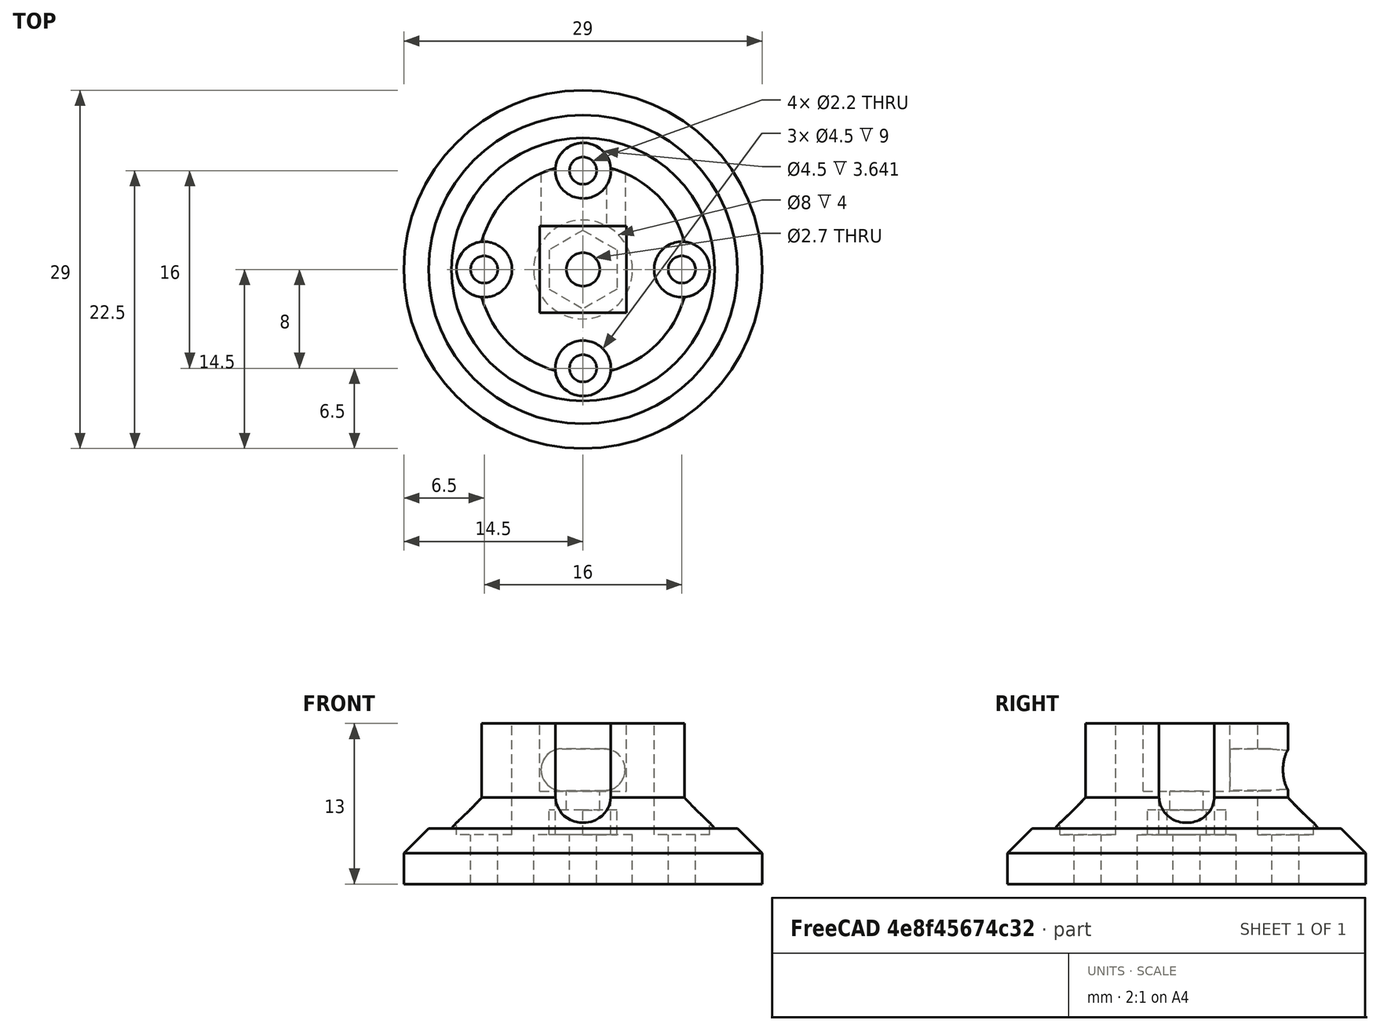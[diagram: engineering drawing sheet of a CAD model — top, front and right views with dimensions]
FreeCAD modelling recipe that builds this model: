
FCSTD DOCUMENT  (FreeCAD 0.14R2935 (Git))
Label: tendon_wheel_ax_9_15_mm
License: CC-BY 3.0
LicenseURL: http://creativecommons.org/licenses/by/3.0/
objects: Part::Cylinder×14, Part::MultiFuse×6, Part::Box×2, Part::Cone×1, Part::Extrusion×1, Part::Mirroring×1, Part::Cut×1, Part::Chamfer×1
note: 27 computed .brp shape members not serialized (recipe doc carries the construction recipe); baked Part::Feature solids carry a one-line shape summary decoded from their .brp

FEATURE [Part::Cylinder] Cylinder
  Angle = 360
  Height = 4.5
  Placement = pos=(0,0,0.5) rot=(0,0,1;0rad)
  Radius = 14.5
FEATURE [Part::Cone] Cone
  Angle = 360
  Height = 3.5
  Placement = pos=(0,0,4) rot=(0,0,1;0rad)
  Radius1 = 11.5
  Radius2 = 8.5
FEATURE [Part::Cylinder] Cylinder001
  Angle = 360
  Height = 6.5
  Placement = pos=(0,0,7) rot=(0,0,1;0rad)
  Radius = 8.5
FEATURE [Part::Cylinder] Cylinder003  label="TopHole003"
  Angle = 360
  Height = 20
  Placement = pos=(-8,0,-3) rot=(0,0,1;0rad)
  Radius = 1.1
FEATURE [Part::Cylinder] Cylinder004  label="TopHole002"
  Angle = 360
  Height = 20
  Placement = pos=(0,-8,-3) rot=(0,0,1;0rad)
  Radius = 1.1
FEATURE [Part::Cylinder] Cylinder005  label="TopHole001"
  Angle = 360
  Height = 20
  Placement = pos=(8,0,-3) rot=(0,0,1;0rad)
  Radius = 1.1
FEATURE [Part::Cylinder] Cylinder006  label="TopHole"
  Angle = 360
  Height = 10
  Placement = pos=(0,8,-3) rot=(0,0,1;0rad)
  Radius = 1.1
FEATURE [Part::Cylinder] Cylinder007  label="TopHole004"
  Angle = 360
  Height = 20
  Placement = pos=(-8,0,3.5) rot=(0,0,1;0rad)
  Radius = 2.25
FEATURE [Part::Cylinder] Cylinder008  label="TopHole005"
  Angle = 360
  Height = 20
  Placement = pos=(8,0,3.5) rot=(0,0,1;0rad)
  Radius = 2.25
FEATURE [Part::Cylinder] Cylinder009  label="TopHole006"
  Angle = 360
  Height = 20
  Placement = pos=(0,8,3.5) rot=(0,0,1;0rad)
  Radius = 2.25
FEATURE [Part::Cylinder] Cylinder010  label="TopHole007"
  Angle = 360
  Height = 20
  Placement = pos=(0,-8,3.5) rot=(0,0,1;0rad)
  Radius = 2.25
FEATURE [Part::MultiFuse] Fusion001
  Placement = pos=(0,0,1) rot=(0,0,1;0rad)
  Shapes = -> [Cylinder010,Cylinder007,Cylinder005,Cylinder003,Cylinder009,Cylinder004,Cylinder008,Cylinder006]
FEATURE [Part::Cylinder] Cylinder012  label="Cylinder003"
  Angle = 360
  Height = 10
  Placement = pos=(-1.7,12,9.75) rot=(1,0,0;1.5708rad)
  Radius = 1.7
FEATURE [Part::Cylinder] Cylinder013  label="Cylinder004"
  Angle = 360
  Height = 20
  Placement = pos=(0,0,-5) rot=(0,0,1;0rad)
  Radius = 1.35
FEATURE [Part::Box] Box  label="Cube"
  Height = 8
  Length = 7
  Placement = pos=(-3.5,-3.5,8) rot=(0,0,1;0rad)
  Width = 7
FEATURE [Part::Extrusion] Extrude
  Dir = (0,0,2)
  Solid = true
FEATURE [Part::Mirroring] Part__Mirroring  label="Extrude (Mirror #1)"
  Base = (0,0,0)
  Normal = (1,0,0)
  Source = -> Extrude
FEATURE [Part::MultiFuse] Fusion002
  Placement = pos=(0,0,4.5) rot=(0,0,1;0rad)
  Shapes = -> [Part__Mirroring,Extrude]
FEATURE [Part::Cylinder] Cylinder014  label="Cylinder005"
  Angle = 360
  Height = 4.5
  Radius = 4
FEATURE [Part::Cylinder] Cylinder015  label="Cylinder006"
  Angle = 360
  Height = 10
  Placement = pos=(1.7,12,9.75) rot=(1,0,0;1.5708rad)
  Radius = 1.7
FEATURE [Part::Box] Box001  label="Cube001"
  Height = 3.4
  Length = 3.6
  Placement = pos=(-1.7,2,8.05) rot=(0,0,1;0rad)
  Width = 10
FEATURE [Part::MultiFuse] Fusion
  Shapes = -> [Cylinder,Cone,Cylinder001]
FEATURE [Part::MultiFuse] Fusion005
  Shapes = -> [Cylinder014,Fusion002,Cylinder013,Fusion001]
FEATURE [Part::MultiFuse] Fusion006
  Shapes = -> [Cylinder015,Box001,Cylinder012,Box]
FEATURE [Part::MultiFuse] Fusion007
  Shapes = -> [Fusion006,Fusion005]
FEATURE [Part::Cut] Cut
  Base = -> Fusion
  Tool = -> Fusion007
FEATURE [Part::Chamfer] Chamfer
  Base = -> Cut
  Edges = 1 edges r=2: [Edge93]
